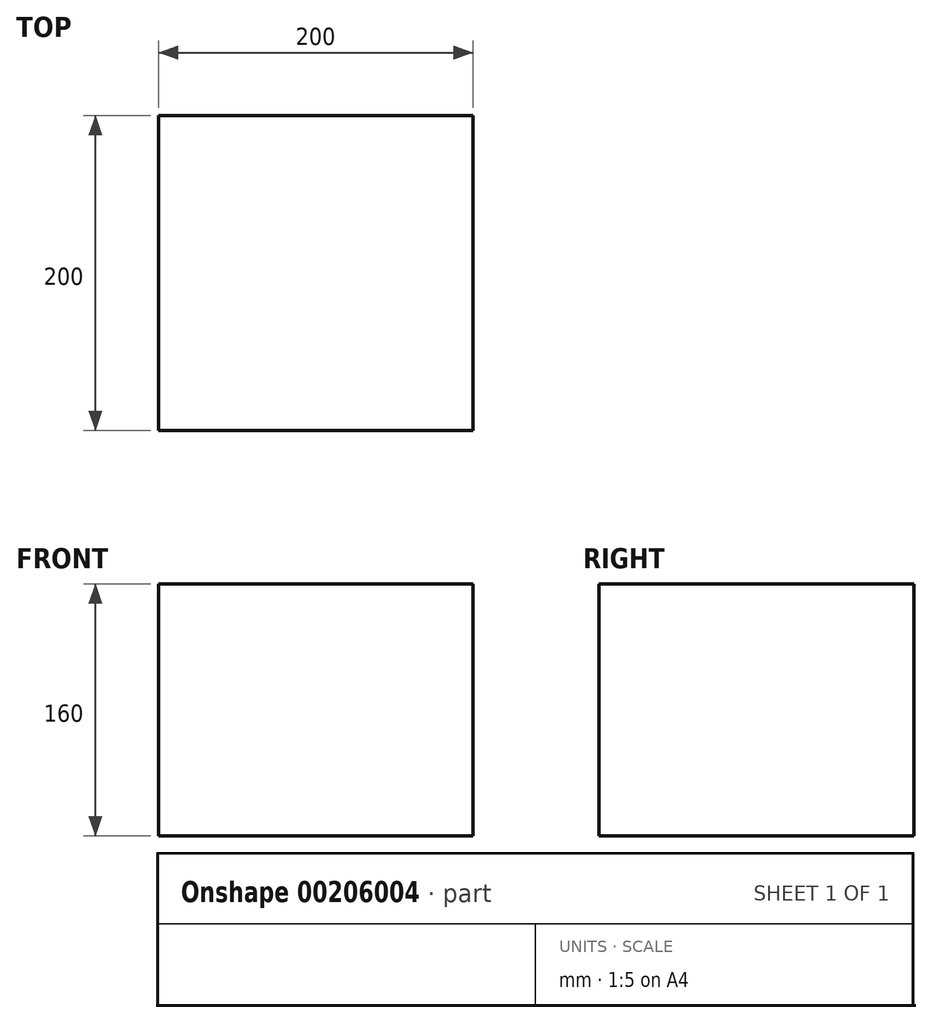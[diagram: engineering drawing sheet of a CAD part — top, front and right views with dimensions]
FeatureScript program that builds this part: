
annotation { "Feature Type Name" : "Feature", "Feature Type Description" : "" }
export const myFeature = defineFeature(function(context is Context, id is Id, definition is map)
    precondition{}
    {
        {
            var Q0;
            Q0=qCreatedBy(makeId("Top.planeOp"),FACE);
            var sketch = newSketch(context, id + "F0", { "sketchPlane" : qUnion([Q0])});
            skLineSegment(sketch, "E0.bottom", {"start": v(0, 200) * mm, "end": v(200, 200) * mm});
            skLineSegment(sketch, "E0.top", {"start": v(0, 0) * mm, "end": v(200, 0) * mm});
            skLineSegment(sketch, "E0.left", {"start": v(0, 200) * mm, "end": v(0, 0) * mm});
            skLineSegment(sketch, "E0.right", {"start": v(200, 200) * mm, "end": v(200, 0) * mm});
            skSolve(sketch);
        }
        {
            var Q0;
            Q0=makeQuery(id+"F0.imprint","IMPRINT",FACE,{"disambiguationData":[TD([[makeQuery(id+"F0.imprint","IMPRINT",EDGE,{"derivedFrom":sQuery(id+"F0.wireOp",EDGE,"E0.bottom")}),-1.0]])]});
            extrude(context, id + "F1", {"entities" : qUnion([Q0]), "depth" : 160 * mm});
        }
    });
